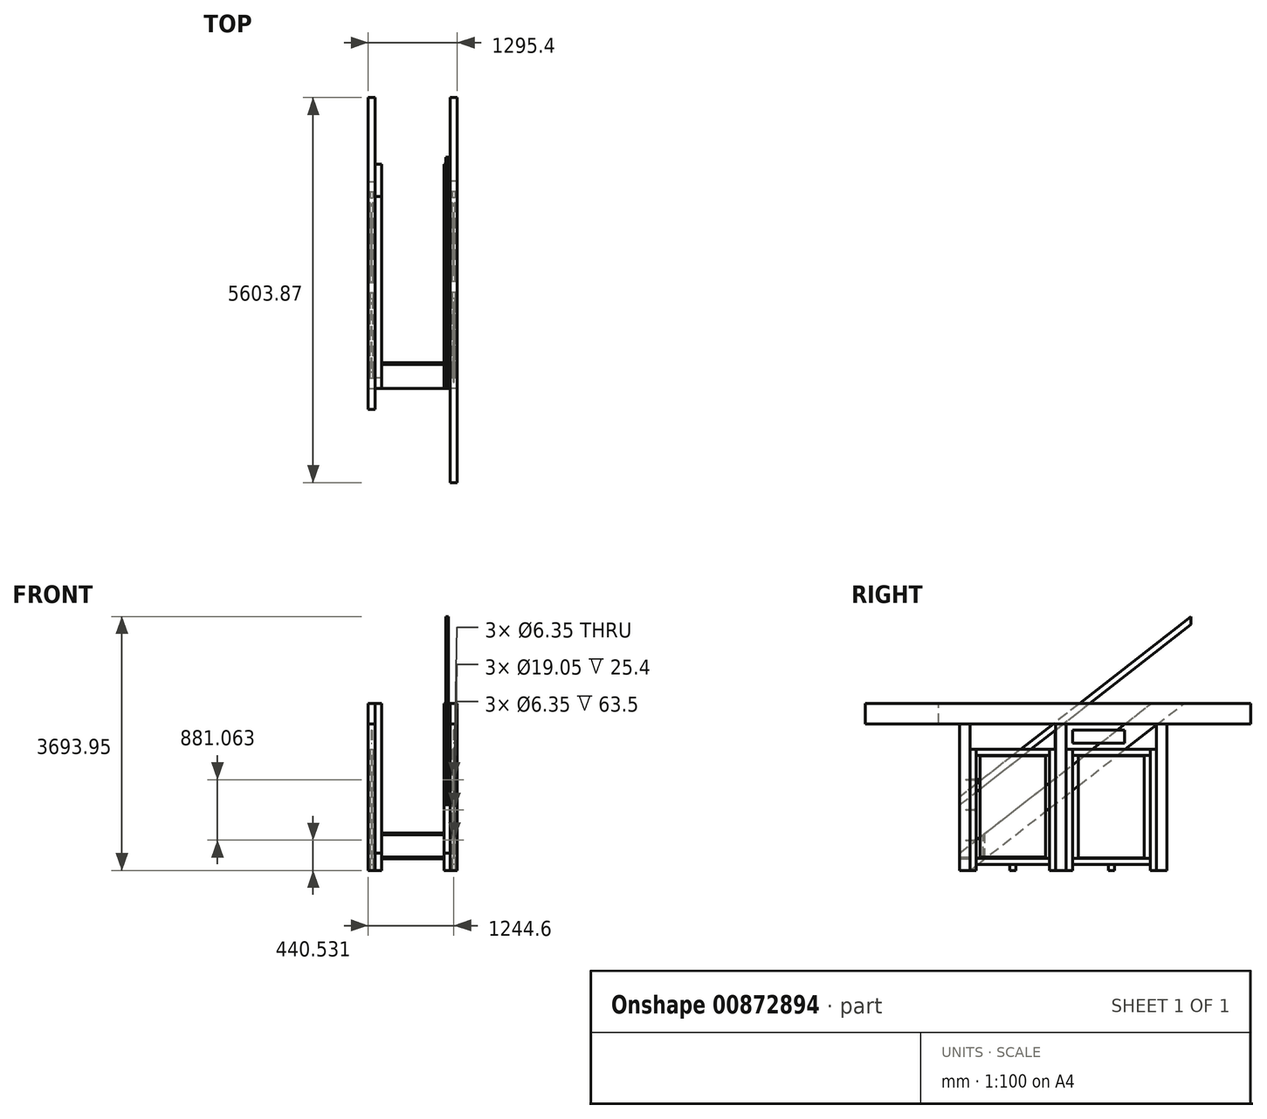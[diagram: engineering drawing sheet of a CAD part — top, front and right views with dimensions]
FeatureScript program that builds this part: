
annotation { "Feature Type Name" : "Feature", "Feature Type Description" : "" }
export const myFeature = defineFeature(function(context is Context, id is Id, definition is map)
    precondition{}
    {
        {
            var Q0;
            Q0=qCreatedBy(makeId("Front.planeOp"),FACE);
            var sketch = newSketch(context, id + "F0", { "sketchPlane" : qUnion([Q0])});
            skLineSegment(sketch, "E0", {"start": v(-546.1, 0) * mm, "end": v(546.1, 0) * mm});
            skSolve(sketch);
        }
        {
            var Q0;
            Q0=sQuery(id+"F0.wireOp",VERTEX,"E0.end");
            var Q1;
            Q1=qCreatedBy(makeId("Right.planeOp"),FACE);
            cPlane(context, id + "F1", {"entities" : qUnion([Q0, Q1]), "cplaneType" : CPlaneType.PLANE_POINT, "offset" : 25.4 * mm, "width" : 152.4 * mm, "height" : 152.4 * mm});
        }
        {
            var Q0;
            Q0=qCreatedBy(id+"F1.planeOp",FACE);
            var sketch = newSketch(context, id + "F2", { "sketchPlane" : qUnion([Q0])});
            skLineSegment(sketch, "E1.bottom", {"start": v(0, 0) * mm, "end": v(152.4, 0) * mm});
            skLineSegment(sketch, "E1.top", {"start": v(0, 2133.6) * mm, "end": v(152.4, 2133.6) * mm});
            skLineSegment(sketch, "E1.left", {"start": v(0, 0) * mm, "end": v(0, 2133.6) * mm});
            skLineSegment(sketch, "E1.right", {"start": v(152.4, 0) * mm, "end": v(152.4, 2133.6) * mm});
            skLineSegment(sketch, "E2.bottom", {"start": v(1397, 0) * mm, "end": v(1552.58, 0) * mm});
            skLineSegment(sketch, "E2.top", {"start": v(1397, 2133.6) * mm, "end": v(1552.57, 2133.6) * mm});
            skLineSegment(sketch, "E2.left", {"start": v(1397, 0) * mm, "end": v(1397, 2133.6) * mm});
            skLineSegment(sketch, "E2.right", {"start": v(1552.58, 0) * mm, "end": v(1552.57, 2133.6) * mm});
            skLineSegment(sketch, "E3.bottom", {"start": v(2860.68, 0) * mm, "end": v(3013.08, 0) * mm});
            skLineSegment(sketch, "E3.top", {"start": v(2860.68, 2133.6) * mm, "end": v(3013.07, 2133.6) * mm});
            skLineSegment(sketch, "E3.left", {"start": v(2860.68, 0) * mm, "end": v(2860.68, 2133.6) * mm});
            skLineSegment(sketch, "E3.right", {"start": v(3013.08, 0) * mm, "end": v(3013.07, 2133.6) * mm});
            skLineSegment(sketch, "E4.bottom", {"start": v(-1371.6, 2432.05) * mm, "end": v(4232.28, 2432.05) * mm});
            skLineSegment(sketch, "E4.top", {"start": v(-1371.6, 2133.6) * mm, "end": v(4232.28, 2133.6) * mm, "construction": true});
            skLineSegment(sketch, "E4.left", {"start": v(-1371.6, 2432.05) * mm, "end": v(-1371.6, 2133.6) * mm});
            skLineSegment(sketch, "E4.right", {"start": v(4232.28, 2432.05) * mm, "end": v(4232.28, 2133.6) * mm});
            skSolve(sketch);
        }
        {
            var Q0;
            Q0=qSketchRegion(id+"F2",true);
            extrude(context, id + "F3", {"entities" : qUnion([Q0]), "depth" : 101.6 * mm, "offsetDistance" : 25.4 * mm});
        }
        {
            var Q0;
            Q0=sQuery(id+"F0.wireOp",VERTEX,"E0.start");
            var Q1;
            Q1=qCreatedBy(makeId("Right.planeOp"),FACE);
            cPlane(context, id + "F4", {"entities" : qUnion([Q0, Q1]), "cplaneType" : CPlaneType.PLANE_POINT, "offset" : 25.4 * mm, "width" : 152.4 * mm, "height" : 152.4 * mm});
        }
        {
            var Q0;
            Q0=qCreatedBy(id+"F4.planeOp",FACE);
            var sketch = newSketch(context, id + "F5", { "sketchPlane" : qUnion([Q0])});
            skLineSegment(sketch, "E5.bottom", {"start": v(1390.65, 0) * mm, "end": v(1543.05, 0) * mm});
            skLineSegment(sketch, "E5.top", {"start": v(1390.65, 2133.6) * mm, "end": v(1543.05, 2133.6) * mm});
            skLineSegment(sketch, "E5.left", {"start": v(1390.65, 0) * mm, "end": v(1390.65, 2133.6) * mm});
            skLineSegment(sketch, "E5.right", {"start": v(1543.05, 0) * mm, "end": v(1543.05, 2133.6) * mm});
            skLineSegment(sketch, "E6.bottom", {"start": v(2863.85, 0) * mm, "end": v(3009.9, 0) * mm});
            skLineSegment(sketch, "E6.top", {"start": v(2863.85, 2133.6) * mm, "end": v(3009.9, 2133.6) * mm});
            skLineSegment(sketch, "E6.left", {"start": v(2863.85, 0) * mm, "end": v(2863.85, 2133.6) * mm});
            skLineSegment(sketch, "E6.right", {"start": v(3009.9, 0) * mm, "end": v(3009.9, 2133.6) * mm});
            skLineSegment(sketch, "E7.0.0", {"start": v(152.4, 2133.6) * mm, "end": v(0, 2133.6) * mm});
            skLineSegment(sketch, "E7.0.1", {"start": v(0, 2133.6) * mm, "end": v(0, 0) * mm});
            skLineSegment(sketch, "E7.0.2", {"start": v(0, 0) * mm, "end": v(152.4, 0) * mm});
            skLineSegment(sketch, "E7.0.3", {"start": v(152.4, 0) * mm, "end": v(152.4, 2133.6) * mm});
            skSolve(sketch);
        }
        {
            var Q0;
            Q0=qSketchRegion(id+"F5",true);
            extrude(context, id + "F6", {"entities" : qUnion([Q0]), "oppositeDirection" : true, "depth" : 101.6 * mm, "offsetDistance" : 25.4 * mm});
        }
        {
            var Q0;
            Q0=qCreatedBy(id+"F1.planeOp",FACE);
            var sketch = newSketch(context, id + "F7", { "sketchPlane" : qUnion([Q0])});
            skLineSegment(sketch, "E8.0", {"start": v(-1371.6, 2133.6) * mm, "end": v(4232.28, 2133.6) * mm});
            skLineSegment(sketch, "E9.0", {"start": v(-1371.6, 2432.05) * mm, "end": v(-1371.6, 2133.6) * mm});
            skLineSegment(sketch, "E10.0", {"start": v(-1371.6, 2432.05) * mm, "end": v(4232.28, 2432.05) * mm});
            skLineSegment(sketch, "E11.0", {"start": v(4232.28, 2432.05) * mm, "end": v(4232.28, 2133.6) * mm});
            skSolve(sketch);
        }
        {
            var Q0;
            Q0=makeQuery(id+"F7.imprint","IMPRINT",FACE,{"disambiguationData":[TD([[makeQuery(id+"F7.imprint","IMPRINT",EDGE,{"derivedFrom":sQuery(id+"F7.wireOp",EDGE,"E8.0")}),1.0]])]});
            var Q1;
            Q1=makeQuery(id+"F3.opExtrude","CAP_FACE",FACE,{"disambiguationData":[OSD([sQuery(id+"F2.wireOp",EDGE,"E1.bottom"),sQuery(id+"F2.wireOp",EDGE,"E1.top"),sQuery(id+"F2.wireOp",EDGE,"E1.left"),sQuery(id+"F2.wireOp",EDGE,"E1.right")])],"isStart":false});
            extrude(context, id + "F8", {"entities" : qUnion([Q0]), "endBound" : BoundingType.UP_TO_SURFACE, "depth" : 25.4 * mm, "endBoundEntityFace" : qUnion([Q1]), "offsetDistance" : 25.4 * mm});
        }
        {
            var Q0;
            Q0=qCreatedBy(id+"F4.planeOp",FACE);
            var sketch = newSketch(context, id + "F9", { "sketchPlane" : qUnion([Q0])});
            skLineSegment(sketch, "E12.0.0", {"start": v(4232.28, 2432.05) * mm, "end": v(4232.28, 2133.6) * mm});
            skLineSegment(sketch, "E12.0.1", {"start": v(4232.28, 2133.6) * mm, "end": v(-304.8, 2133.6) * mm});
            skLineSegment(sketch, "E12.0.3", {"start": v(-304.8, 2432.05) * mm, "end": v(4232.28, 2432.05) * mm});
            skLineSegment(sketch, "E13", {"start": v(-304.8, 2432.05) * mm, "end": v(-304.8, 2133.6) * mm});
            skPoint(sketch, "E12.0.2.end.orphan", {"position": v(-1371.6, 2432.05) * mm});
            skPoint(sketch, "E14.orphan", {"position": v(-1371.6, 2133.6) * mm});
            skSolve(sketch);
        }
        {
            var Q0;
            Q0=qSketchRegion(id+"F9",true);
            var Q1;
            Q1=makeQuery(id+"F6.opExtrude","CAP_FACE",FACE,{"disambiguationData":[OSD([sQuery(id+"F5.wireOp",EDGE,"E7.0.0"),sQuery(id+"F5.wireOp",EDGE,"E7.0.1"),sQuery(id+"F5.wireOp",EDGE,"E7.0.2"),sQuery(id+"F5.wireOp",EDGE,"E7.0.3")])],"isStart":false});
            extrude(context, id + "F10", {"entities" : qUnion([Q0]), "endBound" : BoundingType.UP_TO_SURFACE, "oppositeDirection" : true, "depth" : 25.4 * mm, "endBoundEntityFace" : qUnion([Q1]), "offsetDistance" : 25.4 * mm});
        }
        {
            var Q0;
            Q0=qCreatedBy(id+"F1.planeOp",FACE);
            var sketch = newSketch(context, id + "F11", { "sketchPlane" : qUnion([Q0])});
            skLineSegment(sketch, "E15.0", {"start": v(0, 0) * mm, "end": v(0, 251.61) * mm});
            skLineSegment(sketch, "E16", {"start": v(0, 251.61) * mm, "end": v(2790.83, 2432.05) * mm});
            skLineSegment(sketch, "E17", {"start": v(152.4, 0) * mm, "end": v(3265.28, 2432.05) * mm});
            skPoint(sketch, "E18.orphan", {"position": v(0, 2133.6) * mm});
            skPoint(sketch, "E19.orphan", {"position": v(152.4, 2133.6) * mm});
            skLineSegment(sketch, "E20.0", {"start": v(0, 0) * mm, "end": v(152.4, 0) * mm});
            skLineSegment(sketch, "E21.0", {"start": v(2790.83, 2432.05) * mm, "end": v(3265.28, 2432.05) * mm});
            skPoint(sketch, "E22.orphan", {"position": v(4232.28, 2432.05) * mm});
            skPoint(sketch, "E23.orphan", {"position": v(-1371.6, 2432.05) * mm});
            skPoint(sketch, "E24.0.end.orphan", {"position": v(3013.07, 2133.6) * mm});
            skPoint(sketch, "E24.0.start.orphan", {"position": v(3013.08, 0) * mm});
            skSolve(sketch);
        }
        {
            var Q0;
            Q0=qSketchRegion(id+"F11",true);
            extrude(context, id + "F12", {"entities" : qUnion([Q0]), "oppositeDirection" : true, "depth" : 92.07 * mm, "offsetDistance" : 25.4 * mm});
        }
        {
            var Q0;
            Q0=makeQuery(id+"F12.opExtrude","SWEPT_BODY",BODY,{"disambiguationData":[OSD([sQuery(id+"F11.wireOp",EDGE,"E15.0"),sQuery(id+"F11.wireOp",EDGE,"E16"),sQuery(id+"F11.wireOp",EDGE,"E17"),sQuery(id+"F11.wireOp",EDGE,"E20.0"),sQuery(id+"F11.wireOp",EDGE,"E21.0")])]});
            var Q1;
            Q1=qCreatedBy(makeId("Right.planeOp"),FACE);
            mirror(context, id + "F13", {"entities" : qUnion([Q0]), "mirrorPlane" : qUnion([Q1])});
        }
        {
            var Q0;
            Q0=makeQuery(id+"F3.opExtrude","CAP_FACE",FACE,{"disambiguationData":[OSD([sQuery(id+"F2.wireOp",EDGE,"E1.bottom"),sQuery(id+"F2.wireOp",EDGE,"E1.top"),sQuery(id+"F2.wireOp",EDGE,"E1.left"),sQuery(id+"F2.wireOp",EDGE,"E1.right")])],"isStart":false});
            var Q1;
            Q1=makeQuery(id+"F2.imprint","IMPRINT",FACE,{"disambiguationData":[TD([[makeQuery(id+"F2.imprint","IMPRINT",EDGE,{"derivedFrom":sQuery(id+"F2.wireOp",EDGE,"E1.bottom")}),1.0]])]});
            cPlane(context, id + "F14", {"entities" : qUnion([Q0, Q1]), "cplaneType" : CPlaneType.MID_PLANE, "offset" : 25.4 * mm, "width" : 152.4 * mm, "height" : 152.4 * mm});
        }
        {
            var Q0;
            Q0=qCreatedBy(id+"F14.planeOp",FACE);
            var sketch = newSketch(context, id + "F15", { "sketchPlane" : qUnion([Q0])});
            skLineSegment(sketch, "E25.bottom", {"start": v(241.3, 1762.12) * mm, "end": v(1308.1, 1762.12) * mm});
            skLineSegment(sketch, "E25.top", {"start": v(241.3, 1673.22) * mm, "end": v(1308.1, 1673.22) * mm});
            skPoint(sketch, "E26.orphan", {"position": v(152.4, 2133.6) * mm});
            skPoint(sketch, "E27.orphan", {"position": v(1397, 2133.6) * mm});
            skPoint(sketch, "E28.orphan", {"position": v(1397, 0) * mm});
            skPoint(sketch, "E29.orphan", {"position": v(152.4, 0) * mm});
            skLineSegment(sketch, "E30.bottom", {"start": v(1552.57, 1762.12) * mm, "end": v(2860.67, 1762.12) * mm, "construction": true});
            skLineSegment(sketch, "E30.top", {"start": v(1552.57, 1673.22) * mm, "end": v(2860.67, 1673.22) * mm, "construction": true});
            skLineSegment(sketch, "E30.left", {"start": v(1552.58, 1762.13) * mm, "end": v(1552.58, 1673.22) * mm, "construction": true});
            skLineSegment(sketch, "E30.right", {"start": v(2860.68, 1762.13) * mm, "end": v(2860.68, 1673.23) * mm, "construction": true});
            skLineSegment(sketch, "E31.bottom", {"start": v(152.4, 177.8) * mm, "end": v(1397, 177.8) * mm, "construction": true});
            skLineSegment(sketch, "E31.top", {"start": v(152.4, 88.9) * mm, "end": v(1397, 88.9) * mm, "construction": true});
            skLineSegment(sketch, "E31.left", {"start": v(152.4, 177.8) * mm, "end": v(152.4, 88.9) * mm, "construction": true});
            skLineSegment(sketch, "E31.right", {"start": v(1397, 177.8) * mm, "end": v(1397, 88.9) * mm, "construction": true});
            skLineSegment(sketch, "E32.bottom", {"start": v(1552.58, 177.8) * mm, "end": v(2860.68, 177.8) * mm, "construction": true});
            skLineSegment(sketch, "E32.top", {"start": v(1552.58, 88.9) * mm, "end": v(2860.68, 88.9) * mm, "construction": true});
            skLineSegment(sketch, "E32.left", {"start": v(1552.58, 177.8) * mm, "end": v(1552.58, 88.9) * mm, "construction": true});
            skLineSegment(sketch, "E32.right", {"start": v(2860.68, 177.8) * mm, "end": v(2860.68, 88.9) * mm, "construction": true});
            skLineSegment(sketch, "E33", {"start": v(2206.63, 1762.13) * mm, "end": v(2206.63, 1673.22) * mm, "construction": true});
            skLineSegment(sketch, "E34", {"start": v(774.7, 1762.12) * mm, "end": v(774.7, 1673.22) * mm, "construction": true});
            skLineSegment(sketch, "E35.bottom", {"start": v(298.45, 1668.46) * mm, "end": v(1250.95, 1668.46) * mm, "construction": true});
            skLineSegment(sketch, "E35.top", {"start": v(298.45, 182.56) * mm, "end": v(1250.95, 182.56) * mm, "construction": true});
            skLineSegment(sketch, "E35.left", {"start": v(298.45, 1668.46) * mm, "end": v(298.45, 182.56) * mm, "construction": true});
            skLineSegment(sketch, "E35.right", {"start": v(1250.95, 1668.46) * mm, "end": v(1250.95, 182.56) * mm, "construction": true});
            skPoint(sketch, "E35.middle", {"position": v(774.7, 925.51) * mm});
            skLineSegment(sketch, "E36", {"start": v(774.7, 1673.22) * mm, "end": v(774.7, 177.8) * mm, "construction": true});
            skLineSegment(sketch, "E37.bottom", {"start": v(1730.38, 1668.46) * mm, "end": v(2682.88, 1668.46) * mm, "construction": true});
            skLineSegment(sketch, "E37.top", {"start": v(1730.38, 182.56) * mm, "end": v(2682.88, 182.56) * mm, "construction": true});
            skLineSegment(sketch, "E37.left", {"start": v(1730.38, 1668.46) * mm, "end": v(1730.38, 182.56) * mm, "construction": true});
            skLineSegment(sketch, "E37.right", {"start": v(2682.88, 1668.46) * mm, "end": v(2682.88, 182.56) * mm, "construction": true});
            skPoint(sketch, "E37.middle", {"position": v(2206.62, 925.51) * mm});
            skLineSegment(sketch, "E38", {"start": v(2206.62, 1673.22) * mm, "end": v(2206.62, 177.8) * mm, "construction": true});
            skLineSegment(sketch, "E39", {"start": v(241.3, 1762.12) * mm, "end": v(241.3, 1673.22) * mm});
            skLineSegment(sketch, "E40", {"start": v(1308.1, 1762.12) * mm, "end": v(1308.1, 1673.23) * mm});
            skLineSegment(sketch, "E41.bottom", {"start": v(241.3, 177.8) * mm, "end": v(1308.1, 177.8) * mm});
            skLineSegment(sketch, "E41.top", {"start": v(241.3, 88.9) * mm, "end": v(1308.1, 88.9) * mm});
            skLineSegment(sketch, "E41.left", {"start": v(241.3, 177.8) * mm, "end": v(241.3, 88.9) * mm});
            skLineSegment(sketch, "E41.right", {"start": v(1308.1, 177.8) * mm, "end": v(1308.1, 88.9) * mm});
            skLineSegment(sketch, "E42.bottom", {"start": v(1641.47, 1762.12) * mm, "end": v(2771.78, 1762.12) * mm});
            skLineSegment(sketch, "E42.top", {"start": v(1641.47, 1673.22) * mm, "end": v(2771.78, 1673.22) * mm});
            skLineSegment(sketch, "E42.left", {"start": v(1641.47, 1762.13) * mm, "end": v(1641.47, 1673.22) * mm});
            skLineSegment(sketch, "E42.right", {"start": v(2771.78, 1762.13) * mm, "end": v(2771.78, 1673.22) * mm});
            skLineSegment(sketch, "E43", {"start": v(1552.57, 1717.67) * mm, "end": v(1641.47, 1717.67) * mm, "construction": true});
            skLineSegment(sketch, "E44", {"start": v(241.3, 1717.67) * mm, "end": v(152.4, 1717.67) * mm, "construction": true});
            skLineSegment(sketch, "E45.bottom", {"start": v(1641.47, 177.8) * mm, "end": v(2771.78, 177.8) * mm});
            skLineSegment(sketch, "E45.top", {"start": v(1641.47, 88.9) * mm, "end": v(2771.78, 88.9) * mm});
            skLineSegment(sketch, "E45.left", {"start": v(2771.78, 177.8) * mm, "end": v(2771.78, 88.9) * mm});
            skLineSegment(sketch, "E45.right", {"start": v(1641.47, 177.8) * mm, "end": v(1641.47, 88.9) * mm});
            skSolve(sketch);
        }
        {
            var Q0;
            Q0=qCreatedBy(makeId("Front.planeOp"),FACE);
            var Q1;
            Q1=sQuery(id+"F15.wireOp",VERTEX,"E35.middle");
            cPlane(context, id + "F16", {"entities" : qUnion([Q0, Q1]), "cplaneType" : CPlaneType.PLANE_POINT, "offset" : 25.4 * mm, "width" : 152.4 * mm, "height" : 152.4 * mm});
        }
        {
            var Q0;
            Q0=qSketchRegion(id+"F15",true);
            extrude(context, id + "F17", {"entities" : qUnion([Q0]), "endBound" : BoundingType.SYMMETRIC, "depth" : 38.1 * mm, "offsetDistance" : 25.4 * mm});
        }
        {
            var Q0;
            Q0=qCreatedBy(id+"F14.planeOp",FACE);
            var sketch = newSketch(context, id + "F18", { "sketchPlane" : qUnion([Q0])});
            skPoint(sketch, "E46.0", {"position": v(2206.62, 1668.46) * mm});
            skPoint(sketch, "E47.0", {"position": v(2206.62, 182.56) * mm});
            skLineSegment(sketch, "E48.bottom", {"start": v(1727.2, 1668.46) * mm, "end": v(2686.05, 1668.46) * mm});
            skLineSegment(sketch, "E48.top", {"start": v(1727.2, 182.56) * mm, "end": v(2686.05, 182.56) * mm});
            skLineSegment(sketch, "E48.left", {"start": v(1727.2, 1668.46) * mm, "end": v(1727.2, 182.56) * mm});
            skLineSegment(sketch, "E48.right", {"start": v(2686.05, 1668.46) * mm, "end": v(2686.05, 182.56) * mm});
            skLineSegment(sketch, "E49.0", {"start": v(298.45, 1668.46) * mm, "end": v(1250.95, 1668.46) * mm});
            skLineSegment(sketch, "E50.0", {"start": v(1250.95, 1668.46) * mm, "end": v(1250.95, 182.56) * mm});
            skLineSegment(sketch, "E51.0", {"start": v(298.45, 182.56) * mm, "end": v(1250.95, 182.56) * mm});
            skLineSegment(sketch, "E52.0", {"start": v(298.45, 1668.46) * mm, "end": v(298.45, 182.56) * mm});
            skSolve(sketch);
        }
        {
            var Q0;
            Q0=qSketchRegion(id+"F18",true);
            extrude(context, id + "F19", {"entities" : qUnion([Q0]), "endBound" : BoundingType.SYMMETRIC, "depth" : 12.7 * mm, "offsetDistance" : 25.4 * mm});
        }
        {
            var Q0;
            Q0=qCreatedBy(id+"F14.planeOp",FACE);
            var sketch = newSketch(context, id + "F20", { "sketchPlane" : qUnion([Q0])});
            skLineSegment(sketch, "E53.bottom", {"start": v(152.4, 1762.12) * mm, "end": v(241.3, 1762.12) * mm});
            skLineSegment(sketch, "E53.top", {"start": v(152.4, 0) * mm, "end": v(241.3, 0) * mm});
            skLineSegment(sketch, "E53.left", {"start": v(152.4, 1762.12) * mm, "end": v(152.4, 0) * mm});
            skLineSegment(sketch, "E53.right", {"start": v(241.3, 1762.12) * mm, "end": v(241.3, 0) * mm});
            skLineSegment(sketch, "E54.MirrorCS", {"start": v(1308.1, 1762.13) * mm, "end": v(1308.1, 0) * mm});
            skLineSegment(sketch, "E55.MirrorCS", {"start": v(1397, 1762.13) * mm, "end": v(1397, 0) * mm});
            skLineSegment(sketch, "E56.MirrorCS", {"start": v(1397, 0) * mm, "end": v(1308.1, 0) * mm});
            skLineSegment(sketch, "E57.MirrorCS", {"start": v(1397, 1762.13) * mm, "end": v(1308.1, 1762.13) * mm});
            skLineSegment(sketch, "E58.bottom", {"start": v(1552.58, 1762.12) * mm, "end": v(1641.47, 1762.12) * mm});
            skLineSegment(sketch, "E58.top", {"start": v(1552.58, 0) * mm, "end": v(1641.47, 0) * mm});
            skLineSegment(sketch, "E58.left", {"start": v(1552.58, 1762.12) * mm, "end": v(1552.58, 0) * mm});
            skLineSegment(sketch, "E58.right", {"start": v(1641.47, 1762.12) * mm, "end": v(1641.47, 0) * mm});
            skLineSegment(sketch, "E59.MirrorCS", {"start": v(2860.67, 1762.12) * mm, "end": v(2771.77, 1762.12) * mm});
            skLineSegment(sketch, "E60.MirrorCS", {"start": v(2860.67, 0) * mm, "end": v(2771.78, 0) * mm});
            skLineSegment(sketch, "E61.MirrorCS", {"start": v(2860.67, 1762.12) * mm, "end": v(2860.67, 0) * mm});
            skLineSegment(sketch, "E62.MirrorCS", {"start": v(2771.78, 1762.12) * mm, "end": v(2771.78, 0) * mm});
            skSolve(sketch);
        }
        {
            var Q0;
            Q0 = qSketchRegion(id + "F20", true);
            var Q1;
            Q1=makeQuery(id+"F17.opExtrude","CAP_FACE",FACE,{"disambiguationData":[OSD([sQuery(id+"F15.wireOp",EDGE,"a3709f8d-ca2d-4c25-8878-044553f98fd6.0"),sQuery(id+"F15.wireOp",EDGE,"71a901a5-f4ca-4055-b09d-0ddb529c3825.0"),sQuery(id+"F15.wireOp",EDGE,"E25.bottom"),sQuery(id+"F15.wireOp",EDGE,"E25.top")])],"isStart":false});
            var Q2;
            Q2=makeQuery(id+"F17.opExtrude","CAP_FACE",FACE,{"disambiguationData":[OSD([sQuery(id+"F15.wireOp",EDGE,"a3709f8d-ca2d-4c25-8878-044553f98fd6.0"),sQuery(id+"F15.wireOp",EDGE,"71a901a5-f4ca-4055-b09d-0ddb529c3825.0"),sQuery(id+"F15.wireOp",EDGE,"E25.bottom"),sQuery(id+"F15.wireOp",EDGE,"E25.top")])],"isStart":true});
            extrude(context, id + "F21", {"entities" : qUnion([Q0]), "endBound" : BoundingType.UP_TO_SURFACE, "depth" : 25.4 * mm, "endBoundEntityFace" : qUnion([Q1]), "offsetDistance" : 25.4 * mm, "hasSecondDirection" : true, "secondDirectionBound" : SecondDirectionBoundingType.UP_TO_SURFACE, "secondDirectionOppositeDirection" : true, "secondDirectionDepth" : 25.4 * mm, "secondDirectionBoundEntityFace" : qUnion([Q2])});
        }
        {
            var Q0;
            Q0=qCreatedBy(makeId("Right.planeOp"),FACE);
            var sketch = newSketch(context, id + "F22", { "sketchPlane" : qUnion([Q0])});
            skLineSegment(sketch, "E63", {"start": v(0, 170.54) * mm, "end": v(370.68, 170.54) * mm});
            skLineSegment(sketch, "E64", {"start": v(370.68, 170.54) * mm, "end": v(370.68, 541.22) * mm});
            skLineSegment(sketch, "E65.0", {"start": v(345.28, 195.94) * mm, "end": v(345.28, 521.37) * mm});
            skLineSegment(sketch, "E66.0", {"start": v(0, 195.94) * mm, "end": v(345.28, 195.94) * mm});
            skLineSegment(sketch, "E67.0", {"start": v(345.28, 521.37) * mm, "end": v(370.68, 541.22) * mm});
            skPoint(sketch, "E68.orphan", {"position": v(2790.83, 2432.05) * mm});
            skPoint(sketch, "E69.orphan", {"position": v(0, 251.61) * mm});
            skLineSegment(sketch, "E70.0", {"start": v(0, 170.54) * mm, "end": v(0, 195.94) * mm});
            skPoint(sketch, "E71.orphan", {"position": v(0, 2133.6) * mm});
            skPoint(sketch, "E72.orphan", {"position": v(0, 0) * mm});
            skSolve(sketch);
        }
        {
            var Q0;
            Q0=qSketchRegion(id+"F22",true);
            extrude(context, id + "F23", {"entities" : qUnion([Q0]), "endBound" : BoundingType.UP_TO_NEXT, "depth" : 25.4 * mm, "offsetDistance" : 25.4 * mm, "hasSecondDirection" : true, "secondDirectionBound" : SecondDirectionBoundingType.UP_TO_NEXT, "secondDirectionOppositeDirection" : true, "secondDirectionDepth" : 25.4 * mm});
        }
        {
            var Q0;
            Q0=makeQuery(id+"F12.opExtrude","CAP_FACE",FACE,{"disambiguationData":[OSD([sQuery(id+"F11.wireOp",EDGE,"E15.0"),sQuery(id+"F11.wireOp",EDGE,"E16"),sQuery(id+"F11.wireOp",EDGE,"E17"),sQuery(id+"F11.wireOp",EDGE,"E20.0"),sQuery(id+"F11.wireOp",EDGE,"E21.0")])],"isStart":false});
            var Q1;
            Q1=makeQuery(id+"F12.opExtrude","CAP_FACE",FACE,{"disambiguationData":[OSD([sQuery(id+"F11.wireOp",EDGE,"E15.0"),sQuery(id+"F11.wireOp",EDGE,"E16"),sQuery(id+"F11.wireOp",EDGE,"E17"),sQuery(id+"F11.wireOp",EDGE,"E20.0"),sQuery(id+"F11.wireOp",EDGE,"E21.0")])],"isStart":true});
            cPlane(context, id + "F24", {"entities" : qUnion([Q0, Q1]), "cplaneType" : CPlaneType.MID_PLANE, "offset" : 25.4 * mm, "width" : 152.4 * mm, "height" : 152.4 * mm});
        }
        {
            var Q0;
            Q0=qCreatedBy(id+"F24.planeOp",FACE);
            var sketch = newSketch(context, id + "F25", { "sketchPlane" : qUnion([Q0])});
            skLineSegment(sketch, "E73", {"start": v(-3362.6, 3693.95) * mm, "end": v(0, 1066.8) * mm});
            skLineSegment(sketch, "E74", {"start": v(0, 1066.8) * mm, "end": v(0, 953.98) * mm});
            skLineSegment(sketch, "E75", {"start": v(0, 953.98) * mm, "end": v(-3362.6, 3581.13) * mm});
            skLineSegment(sketch, "E76", {"start": v(-3362.6, 3693.95) * mm, "end": v(-3362.6, 3581.13) * mm});
            skSolve(sketch);
        }
        {
            var Q0;
            Q0 = qSketchRegion(id + "F25", true);
            extrude(context, id + "F26", {"entities" : qUnion([Q0]), "endBound" : BoundingType.SYMMETRIC, "depth" : 38.1 * mm, "offsetDistance" : 25.4 * mm});
        }
        {
            var Q0;
            Q0=qCreatedBy(id+"F14.planeOp",FACE);
            var sketch = newSketch(context, id + "F27", { "sketchPlane" : qUnion([Q0])});
            skLineSegment(sketch, "E77.bottom", {"start": v(1641.47, 2044.7) * mm, "end": v(2403.48, 2044.7) * mm});
            skLineSegment(sketch, "E77.top", {"start": v(1641.48, 1851.02) * mm, "end": v(2403.47, 1851.02) * mm});
            skLineSegment(sketch, "E77.left", {"start": v(1641.48, 2044.7) * mm, "end": v(1641.48, 1851.03) * mm});
            skLineSegment(sketch, "E77.right", {"start": v(2403.48, 2044.7) * mm, "end": v(2403.48, 1851.03) * mm});
            skLineSegment(sketch, "E78", {"start": v(1641.48, 1947.86) * mm, "end": v(1552.57, 1947.86) * mm, "construction": true});
            skLineSegment(sketch, "E79", {"start": v(2022.47, 1851.02) * mm, "end": v(2022.47, 1762.12) * mm, "construction": true});
            skLineSegment(sketch, "E80", {"start": v(2022.47, 2044.7) * mm, "end": v(2022.47, 2133.6) * mm, "construction": true});
            skSolve(sketch);
        }
        {
            var Q0;
            Q0 = qSketchRegion(id + "F27", true);
            var Q1;
            Q1=makeQuery(id+"F19.opExtrude","CAP_FACE",FACE,{"disambiguationData":[OSD([sQuery(id+"F18.wireOp",EDGE,"E48.bottom"),sQuery(id+"F18.wireOp",EDGE,"E48.top"),sQuery(id+"F18.wireOp",EDGE,"E48.left"),sQuery(id+"F18.wireOp",EDGE,"E48.right")])],"isStart":false});
            var Q2;
            Q2=makeQuery(id+"F19.opExtrude","CAP_FACE",FACE,{"disambiguationData":[OSD([sQuery(id+"F18.wireOp",EDGE,"E49.0"),sQuery(id+"F18.wireOp",EDGE,"E50.0"),sQuery(id+"F18.wireOp",EDGE,"E51.0"),sQuery(id+"F18.wireOp",EDGE,"E52.0")])],"isStart":true});
            extrude(context, id + "F28", {"entities" : qUnion([Q0]), "endBound" : BoundingType.UP_TO_SURFACE, "depth" : 25.4 * mm, "endBoundEntityFace" : qUnion([Q1]), "offsetDistance" : 25.4 * mm, "hasSecondDirection" : true, "secondDirectionBound" : SecondDirectionBoundingType.UP_TO_SURFACE, "secondDirectionOppositeDirection" : true, "secondDirectionDepth" : 25.4 * mm, "secondDirectionBoundEntityFace" : qUnion([Q2])});
        }
        {
            var Q0;
            Q0=qCreatedBy(id+"F1.planeOp",FACE);
            var sketch = newSketch(context, id + "F29", { "sketchPlane" : qUnion([Q0])});
            skLineSegment(sketch, "E81.bottom", {"start": v(730.25, 88.9) * mm, "end": v(819.15, 88.9) * mm});
            skLineSegment(sketch, "E81.top", {"start": v(730.25, 0) * mm, "end": v(819.15, 0) * mm});
            skLineSegment(sketch, "E81.left", {"start": v(730.25, 88.9) * mm, "end": v(730.25, 0) * mm});
            skLineSegment(sketch, "E81.right", {"start": v(819.15, 88.9) * mm, "end": v(819.15, 0) * mm});
            skLineSegment(sketch, "E82", {"start": v(774.7, 88.9) * mm, "end": v(774.7, 177.8) * mm, "construction": true});
            skLineSegment(sketch, "E83.bottom", {"start": v(2162.18, 88.9) * mm, "end": v(2251.07, 88.9) * mm});
            skLineSegment(sketch, "E83.top", {"start": v(2162.18, 0) * mm, "end": v(2251.07, 0) * mm});
            skLineSegment(sketch, "E83.left", {"start": v(2162.18, 88.9) * mm, "end": v(2162.18, 0) * mm});
            skLineSegment(sketch, "E83.right", {"start": v(2251.07, 88.9) * mm, "end": v(2251.07, 0) * mm});
            skLineSegment(sketch, "E84", {"start": v(2206.62, 88.9) * mm, "end": v(2206.62, 177.8) * mm, "construction": true});
            skSolve(sketch);
        }
        {
            var Q0;
            Q0=makeQuery(id+"F17.opExtrude","SWEPT_BODY",BODY,{"disambiguationData":[OSD([sQuery(id+"F15.wireOp",EDGE,"E25.bottom"),sQuery(id+"F15.wireOp",EDGE,"E25.top"),sQuery(id+"F15.wireOp",EDGE,"E39"),sQuery(id+"F15.wireOp",EDGE,"E40")])]});
            var Q1;
            Q1=makeQuery(id+"F21.opExtrude","SWEPT_BODY",BODY,{"disambiguationData":[OSD([sQuery(id+"F20.wireOp",EDGE,"E53.bottom"),sQuery(id+"F20.wireOp",EDGE,"E53.top"),sQuery(id+"F20.wireOp",EDGE,"E53.left"),sQuery(id+"F20.wireOp",EDGE,"E53.right")])]});
            var Q2;
            Q2=makeQuery(id+"F19.opExtrude","SWEPT_BODY",BODY,{"disambiguationData":[OSD([sQuery(id+"F18.wireOp",EDGE,"E49.0"),sQuery(id+"F18.wireOp",EDGE,"E50.0"),sQuery(id+"F18.wireOp",EDGE,"E51.0"),sQuery(id+"F18.wireOp",EDGE,"E52.0")])]});
            var Q3;
            Q3=makeQuery(id+"F21.opExtrude","SWEPT_BODY",BODY,{"disambiguationData":[OSD([sQuery(id+"F20.wireOp",EDGE,"E54.MirrorCS"),sQuery(id+"F20.wireOp",EDGE,"E55.MirrorCS"),sQuery(id+"F20.wireOp",EDGE,"E56.MirrorCS"),sQuery(id+"F20.wireOp",EDGE,"E57.MirrorCS")])]});
            var Q4;
            Q4=makeQuery(id+"F17.opExtrude","SWEPT_BODY",BODY,{"disambiguationData":[OSD([sQuery(id+"F15.wireOp",EDGE,"E41.bottom"),sQuery(id+"F15.wireOp",EDGE,"E41.top"),sQuery(id+"F15.wireOp",EDGE,"E41.left"),sQuery(id+"F15.wireOp",EDGE,"E41.right")])]});
            var Q5;
            Q5=makeQuery(id+"F21.opExtrude","SWEPT_BODY",BODY,{"disambiguationData":[OSD([sQuery(id+"F20.wireOp",EDGE,"E58.bottom"),sQuery(id+"F20.wireOp",EDGE,"E58.top"),sQuery(id+"F20.wireOp",EDGE,"E58.left"),sQuery(id+"F20.wireOp",EDGE,"E58.right")])]});
            var Q6;
            Q6=makeQuery(id+"F17.opExtrude","SWEPT_BODY",BODY,{"disambiguationData":[OSD([sQuery(id+"F15.wireOp",EDGE,"E42.bottom"),sQuery(id+"F15.wireOp",EDGE,"E42.top"),sQuery(id+"F15.wireOp",EDGE,"E42.left"),sQuery(id+"F15.wireOp",EDGE,"E42.right")])]});
            var Q7;
            Q7=makeQuery(id+"F21.opExtrude","SWEPT_BODY",BODY,{"disambiguationData":[OSD([sQuery(id+"F20.wireOp",EDGE,"E59.MirrorCS"),sQuery(id+"F20.wireOp",EDGE,"E60.MirrorCS"),sQuery(id+"F20.wireOp",EDGE,"E61.MirrorCS"),sQuery(id+"F20.wireOp",EDGE,"E62.MirrorCS")])]});
            var Q8;
            Q8=makeQuery(id+"F17.opExtrude","SWEPT_BODY",BODY,{"disambiguationData":[OSD([sQuery(id+"F15.wireOp",EDGE,"E45.bottom"),sQuery(id+"F15.wireOp",EDGE,"E45.top"),sQuery(id+"F15.wireOp",EDGE,"E45.left"),sQuery(id+"F15.wireOp",EDGE,"E45.right")])]});
            var Q9;
            Q9=makeQuery(id+"F19.opExtrude","SWEPT_BODY",BODY,{"disambiguationData":[OSD([sQuery(id+"F18.wireOp",EDGE,"E48.bottom"),sQuery(id+"F18.wireOp",EDGE,"E48.top"),sQuery(id+"F18.wireOp",EDGE,"E48.left"),sQuery(id+"F18.wireOp",EDGE,"E48.right")])]});
            var Q10;
            Q10=makeQuery(id+"F28.opExtrude","SWEPT_BODY",BODY,{"disambiguationData":[OSD([sQuery(id+"F27.wireOp",EDGE,"E77.bottom"),sQuery(id+"F27.wireOp",EDGE,"E77.top"),sQuery(id+"F27.wireOp",EDGE,"E77.left"),sQuery(id+"F27.wireOp",EDGE,"E77.right")])]});
            var Q11;
            Q11=qCreatedBy(makeId("Right.planeOp"),FACE);
            mirror(context, id + "F30", {"entities" : qUnion([Q0, Q1, Q2, Q3, Q4, Q5, Q6, Q7, Q8, Q9, Q10]), "mirrorPlane" : qUnion([Q11])});
        }
        {
            var Q0;
            Q0 = qSketchRegion(id + "F29", true);
            var Q1;
            Q1=makeQuery(id+"F3.opExtrude","CAP_FACE",FACE,{"disambiguationData":[OSD([sQuery(id+"F2.wireOp",EDGE,"E2.bottom"),sQuery(id+"F2.wireOp",EDGE,"E2.top"),sQuery(id+"F2.wireOp",EDGE,"E2.left"),sQuery(id+"F2.wireOp",EDGE,"E2.right")])],"isStart":false});
            extrude(context, id + "F31", {"entities" : qUnion([Q0]), "endBound" : BoundingType.UP_TO_SURFACE, "depth" : 25.4 * mm, "endBoundEntityFace" : qUnion([Q1]), "offsetDistance" : 25.4 * mm});
        }
        {
            var Q0;
            Q0=makeQuery(id+"F21.opExtrude","SWEPT_FACE",FACE,{"disambiguationData":[OSD([sQuery(id+"F20.wireOp",EDGE,"E53.right")])]});
            var sketch = newSketch(context, id + "F32", { "sketchPlane" : qUnion([Q0])});
            skLineSegment(sketch, "E85", {"start": v(-596.9, 1762.12) * mm, "end": v(-596.9, 1321.6) * mm, "construction": true});
            skLineSegment(sketch, "E86", {"start": v(-596.9, 1321.6) * mm, "end": v(-596.9, 881.06) * mm, "construction": true});
            skLineSegment(sketch, "E87", {"start": v(-596.9, 881.06) * mm, "end": v(-596.9, 440.53) * mm, "construction": true});
            skLineSegment(sketch, "E88", {"start": v(-596.9, 440.53) * mm, "end": v(-596.9, 0) * mm, "construction": true});
            skCircle(sketch, "E89", {"center": v(-596.9, 1321.6) * mm, "radius": 3.18 * mm});
            skCircle(sketch, "E90", {"center": v(-596.9, 881.06) * mm, "radius": 3.18 * mm});
            skCircle(sketch, "E91", {"center": v(-596.9, 440.53) * mm, "radius": 3.17 * mm});
            skSolve(sketch);
        }
        {
            var Q0;
            Q0 = qSketchRegion(id + "F32", true);
            var Q1;
            Q1=makeQuery(id+"F21.opExtrude","SWEPT_FACE",FACE,{"disambiguationData":[OSD([sQuery(id+"F20.wireOp",EDGE,"E53.left")])]});
            extrude(context, id + "F33", {"entities" : qUnion([Q0]), "operationType" : NewBodyOperationType.REMOVE, "oppositeDirection" : true, "depth" : 152.4 * mm, "endBoundEntityFace" : qUnion([Q1]), "offsetDistance" : 25.4 * mm});
        }
        {
            var Q0;
            Q0=makeQuery(id+"F32.imprint","IMPRINT",FACE,{"disambiguationData":[TD([[makeQuery(id+"F32.imprint","IMPRINT",EDGE,{"derivedFrom":sQuery(id+"F32.wireOp",EDGE,"E89")}),-1.0]])]});
            var sketch = newSketch(context, id + "F34", { "sketchPlane" : qUnion([Q0])});
            skCircle(sketch, "E92", {"center": v(-596.9, 1321.6) * mm, "radius": 9.53 * mm});
            skCircle(sketch, "E93", {"center": v(-596.9, 881.06) * mm, "radius": 9.53 * mm});
            skCircle(sketch, "E94", {"center": v(-596.9, 440.53) * mm, "radius": 9.53 * mm});
            skSolve(sketch);
        }
        {
            var Q0;
            Q0 = qSketchRegion(id + "F34", true);
            extrude(context, id + "F35", {"entities" : qUnion([Q0]), "operationType" : NewBodyOperationType.REMOVE, "oppositeDirection" : true, "depth" : 25.4 * mm, "offsetDistance" : 25.4 * mm});
        }
        {
            var Q0;
            Q0=makeQuery(id+"F21.opExtrude","SWEPT_FACE",FACE,{"disambiguationData":[OSD([sQuery(id+"F20.wireOp",EDGE,"E53.left")])]});
            var sketch = newSketch(context, id + "F36", { "sketchPlane" : qUnion([Q0])});
            skCircle(sketch, "E95.0", {"center": v(596.9, 1321.6) * mm, "radius": 3.18 * mm});
            skSolve(sketch);
        }
        {
            var Q0;
            Q0 = qSketchRegion(id + "F36", true);
            extrude(context, id + "F37", {"entities" : qUnion([Q0]), "oppositeDirection" : true, "depth" : 127 * mm, "offsetDistance" : 25.4 * mm});
        }
        {
            var Q0;
            Q0=makeQuery(id+"F37.opExtrude","CAP_FACE",FACE,{"disambiguationData":[OSD([sQuery(id+"F36.wireOp",EDGE,"E95.0")])],"isStart":false});
            var sketch = newSketch(context, id + "F38", { "sketchPlane" : qUnion([Q0])});
            skCircle(sketch, "E96", {"center": v(-596.9, 1321.6) * mm, "radius": 5.56 * mm, "construction": true});
            skLineSegment(sketch, "E97.0", {"start": v(-600.1, 1327.15) * mm, "end": v(-593.7, 1327.15) * mm});
            skLineSegment(sketch, "E97.1", {"start": v(-593.7, 1327.15) * mm, "end": v(-590.48, 1321.6) * mm});
            skLineSegment(sketch, "E97.2", {"start": v(-590.48, 1321.6) * mm, "end": v(-593.7, 1316.04) * mm});
            skLineSegment(sketch, "E97.3", {"start": v(-593.7, 1316.04) * mm, "end": v(-600.1, 1316.04) * mm});
            skLineSegment(sketch, "E97.4", {"start": v(-600.1, 1316.04) * mm, "end": v(-603.32, 1321.6) * mm});
            skLineSegment(sketch, "E97.5", {"start": v(-603.32, 1321.6) * mm, "end": v(-600.1, 1327.15) * mm});
            skPoint(sketch, "E97.0.midPoint", {"position": v(-596.9, 1327.15) * mm});
            skSolve(sketch);
        }
        {
            var Q0;
            Q0 = qSketchRegion(id + "F38", true);
            extrude(context, id + "F39", {"entities" : qUnion([Q0]), "operationType" : NewBodyOperationType.ADD, "oppositeDirection" : true, "depth" : 4.37 * mm, "offsetDistance" : 25.4 * mm});
        }
        {
            var Q0;
            Q0=qCreatedBy(id+"F16.planeOp",FACE);
            var sketch = newSketch(context, id + "F40", { "sketchPlane" : qUnion([Q0])});
            skLineSegment(sketch, "E98.0", {"start": v(606.42, 177.8) * mm, "end": v(587.38, 177.8) * mm});
            skLineSegment(sketch, "E99", {"start": v(596.9, 177.8) * mm, "end": v(596.9, 196.85) * mm, "construction": true});
            skLineSegment(sketch, "E100", {"start": v(606.42, 177.8) * mm, "end": v(606.42, 196.85) * mm});
            skLineSegment(sketch, "E101", {"start": v(606.42, 196.85) * mm, "end": v(604.9, 196.85) * mm});
            skLineSegment(sketch, "E102", {"start": v(604.9, 196.85) * mm, "end": v(604.9, 179.32) * mm});
            skLineSegment(sketch, "E103.MirrorCS", {"start": v(587.38, 177.8) * mm, "end": v(587.38, 196.85) * mm});
            skLineSegment(sketch, "E104.MirrorCS", {"start": v(587.38, 196.85) * mm, "end": v(588.9, 196.85) * mm});
            skLineSegment(sketch, "E105.MirrorCS", {"start": v(588.9, 196.85) * mm, "end": v(588.9, 179.32) * mm});
            skLineSegment(sketch, "E106", {"start": v(604.9, 179.32) * mm, "end": v(588.9, 179.32) * mm});
            skPoint(sketch, "E107.orphan", {"position": v(615.95, 177.8) * mm});
            skPoint(sketch, "E108.orphan", {"position": v(577.85, 177.8) * mm});
            skSolve(sketch);
        }
        {
            var Q0;
            Q0=makeQuery(id+"F40.imprint","IMPRINT",FACE,{"disambiguationData":[TD([[makeQuery(id+"F40.imprint","IMPRINT",EDGE,{"derivedFrom":sQuery(id+"F40.wireOp",EDGE,"E98.0")}),-1.0]])]});
            var Q1;
            Q1=makeQuery(id+"F19.opExtrude","SWEPT_FACE",FACE,{"disambiguationData":[OSD([sQuery(id+"F18.wireOp",EDGE,"E50.0")])]});
            var Q2;
            Q2=makeQuery(id+"F19.opExtrude","SWEPT_FACE",FACE,{"disambiguationData":[OSD([sQuery(id+"F18.wireOp",EDGE,"E52.0")])]});
            extrude(context, id + "F41", {"entities" : qUnion([Q0]), "endBound" : BoundingType.UP_TO_SURFACE, "oppositeDirection" : true, "depth" : 914.4 * mm, "endBoundEntityFace" : qUnion([Q1]), "offsetDistance" : 25.4 * mm, "hasSecondDirection" : true, "secondDirectionBound" : SecondDirectionBoundingType.UP_TO_SURFACE, "secondDirectionOppositeDirection" : false, "secondDirectionDepth" : 25.4 * mm, "secondDirectionBoundEntityFace" : qUnion([Q2])});
        }
        {
            var Q0;
            Q0=qCreatedBy(id+"F16.planeOp",FACE);
            var sketch = newSketch(context, id + "F42", { "sketchPlane" : qUnion([Q0])});
            skLineSegment(sketch, "E109.0", {"start": v(604.9, 196.85) * mm, "end": v(604.9, 179.32) * mm});
            skLineSegment(sketch, "E110.0", {"start": v(604.9, 179.32) * mm, "end": v(588.9, 179.32) * mm});
            skLineSegment(sketch, "E111.0", {"start": v(588.9, 196.85) * mm, "end": v(588.9, 179.32) * mm});
            skLineSegment(sketch, "E112", {"start": v(604.9, 195.2) * mm, "end": v(603.25, 195.2) * mm});
            skLineSegment(sketch, "E113", {"start": v(603.25, 195.2) * mm, "end": v(603.25, 182.5) * mm});
            skLineSegment(sketch, "E114.MirrorCS", {"start": v(588.9, 195.2) * mm, "end": v(590.55, 195.2) * mm});
            skLineSegment(sketch, "E115.MirrorCS", {"start": v(590.55, 195.2) * mm, "end": v(590.55, 182.5) * mm});
            skLineSegment(sketch, "E116", {"start": v(603.25, 182.5) * mm, "end": v(590.55, 182.5) * mm});
            skSolve(sketch);
        }
        {
            var Q0;
            Q0 = qSketchRegion(id + "F42", true);
            var Q1;
            Q1=makeQuery(id+"F19.opExtrude","SWEPT_FACE",FACE,{"disambiguationData":[OSD([sQuery(id+"F18.wireOp",EDGE,"E52.0")])]});
            var Q2;
            Q2=makeQuery(id+"F19.opExtrude","SWEPT_FACE",FACE,{"disambiguationData":[OSD([sQuery(id+"F18.wireOp",EDGE,"E50.0")])]});
            extrude(context, id + "F43", {"entities" : qUnion([Q0]), "endBound" : BoundingType.UP_TO_SURFACE, "depth" : 25.4 * mm, "endBoundEntityFace" : qUnion([Q1]), "offsetDistance" : 25.4 * mm, "hasSecondDirection" : true, "secondDirectionBound" : SecondDirectionBoundingType.UP_TO_SURFACE, "secondDirectionOppositeDirection" : true, "secondDirectionDepth" : 25.4 * mm, "secondDirectionBoundEntityFace" : qUnion([Q2])});
        }
    });
